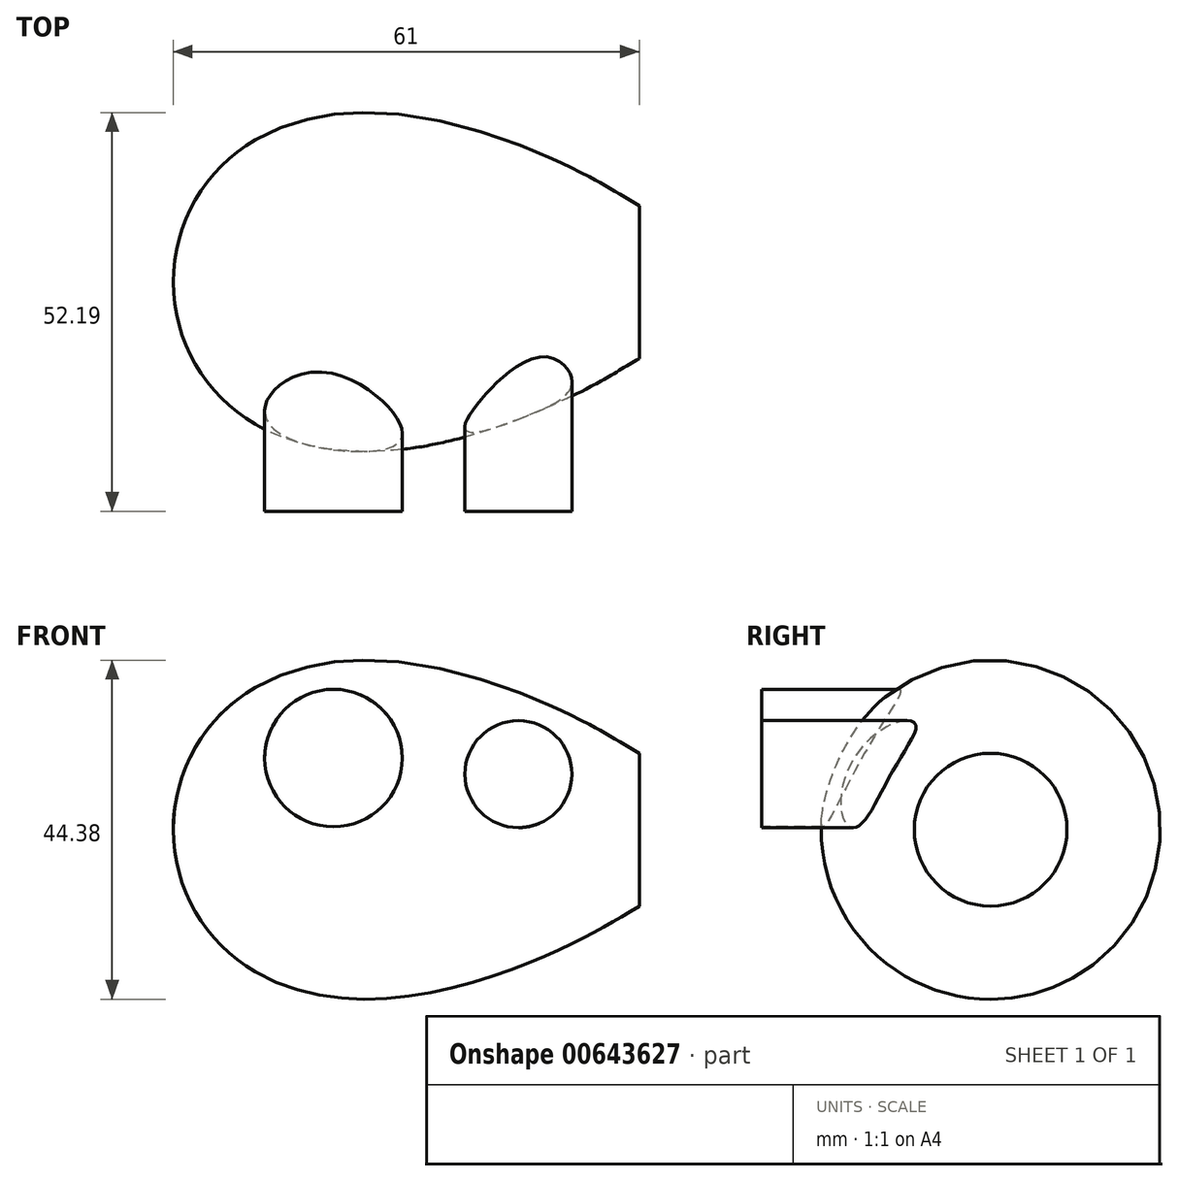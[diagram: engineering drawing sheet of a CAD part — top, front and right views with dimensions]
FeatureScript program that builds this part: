
annotation { "Feature Type Name" : "Feature", "Feature Type Description" : "" }
export const myFeature = defineFeature(function(context is Context, id is Id, definition is map)
    precondition{}
    {
        {
            var Q0;
            Q0=qCreatedBy(makeId("Front.planeOp"),FACE);
            var sketch = newSketch(context, id + "F0", { "sketchPlane" : qUnion([Q0])});
            skLineSegment(sketch, "E0", {"start": v(0, 0) * mm, "end": v(0, 10) * mm});
            skArc(sketch, "E1", {"start": v(-50.25, 18.62) * mm, "mid": v(-58.12, 10.75) * mm, "end": v(-61, 0) * mm});
            skLineSegment(sketch, "E2", {"start": v(0, 0) * mm, "end": v(-61, 0) * mm});
            skLineSegment(sketch, "E3", {"start": v(-50.25, 18.62) * mm, "end": v(-39.5, 0) * mm, "construction": true});
            skFitSpline(sketch, "E4", {"points": [v(-50.25, 18.62) * mm, v(-11.06, 15.98) * mm, v(0, 10) * mm], "startDerivative": vector(61.2, 35.33) * mm, "endDerivative": vector(27.67, -16.4) * mm});
            skLineSegment(sketch, "E5", {"start": v(-39.5, 0) * mm, "end": v(-39.5, 22) * mm, "construction": true});
            skLineSegment(sketch, "E6", {"start": v(-50.25, 18.62) * mm, "end": v(-50.25, 0) * mm, "construction": true});
            skSolve(sketch);
        }
        {
            var Q0;
            Q0 = qSketchRegion(id + "F0", true);
            var Q1;
            Q1=sQuery(id+"F0.wireOp",EDGE,"E2");
            revolve(context, id + "F1", {"entities" : qUnion([Q0]), "axis" : qUnion([Q1]), "revolveType" : RevolveType.FULL});
        }
        {
            var Q0;
            Q0=qCreatedBy(makeId("Front.planeOp"),FACE);
            cPlane(context, id + "F2", {"entities" : qUnion([Q0]), "cplaneType" : CPlaneType.OFFSET, "offset" : 30 * mm, "width" : 152.4 * mm, "height" : 152.4 * mm});
        }
        {
            var Q0;
            Q0=qCreatedBy(id+"F2.planeOp",FACE);
            var sketch = newSketch(context, id + "F3", { "sketchPlane" : qUnion([Q0])});
            skCircle(sketch, "E7", {"center": v(-40.03, 9.38) * mm, "radius": 9 * mm});
            skCircle(sketch, "E8", {"center": v(-15.82, 7.27) * mm, "radius": 7 * mm});
            skSolve(sketch);
        }
        {
            var Q0;
            Q0=makeQuery(id+"F3.imprint","IMPRINT",FACE,{"disambiguationData":[TD([[makeQuery(id+"F3.imprint","IMPRINT",EDGE,{"derivedFrom":sQuery(id+"F3.wireOp",EDGE,"E8")}),1.0]])]});
            var Q1;
            Q1=makeQuery(id+"F3.imprint","IMPRINT",FACE,{"disambiguationData":[TD([[makeQuery(id+"F3.imprint","IMPRINT",EDGE,{"derivedFrom":sQuery(id+"F3.wireOp",EDGE,"E7")}),1.0]])]});
            extrude(context, id + "F4", {"entities" : qUnion([Q0, Q1]), "operationType" : NewBodyOperationType.ADD, "endBound" : BoundingType.UP_TO_NEXT, "oppositeDirection" : true, "depth" : 25.4 * mm, "offsetDistance" : 25.4 * mm});
        }
        {
            var Q0;
            Q0=sQuery(id+"F0.wireOp",VERTEX,"E6.end");
            var Q1;
            Q1=sQuery(id+"F0.wireOp",EDGE,"E2");
            cPlane(context, id + "F5", {"entities" : qUnion([Q0, Q1]), "cplaneType" : CPlaneType.LINE_POINT, "offset" : 25.4 * mm, "width" : 152.4 * mm, "height" : 152.4 * mm});
        }
        {
            var Q0;
            Q0=qCreatedBy(id+"F5.planeOp",FACE);
            var sketch = newSketch(context, id + "F6", { "sketchPlane" : qUnion([Q0])});
            skLineSegment(sketch, "E9", {"start": v(0, 0) * mm, "end": v(16.12, -9.3) * mm, "construction": true});
            skLineSegment(sketch, "E10", {"start": v(0, 0) * mm, "end": v(18.62, 0) * mm, "construction": true});
            skSolve(sketch);
        }
        {
            var Q0;
            Q0=sQuery(id+"F0.wireOp",VERTEX,"E5.end");
            var Q1;
            Q1=sQuery(id+"F0.wireOp",VERTEX,"E5.start");
            var Q2;
            Q2=sQuery(id+"F6.wireOp",VERTEX,"E9.end");
            cPlane(context, id + "F7", {"entities" : qUnion([Q0, Q1, Q2]), "cplaneType" : CPlaneType.THREE_POINT, "offset" : 25.4 * mm, "width" : 152.4 * mm, "height" : 152.4 * mm});
        }
    });
